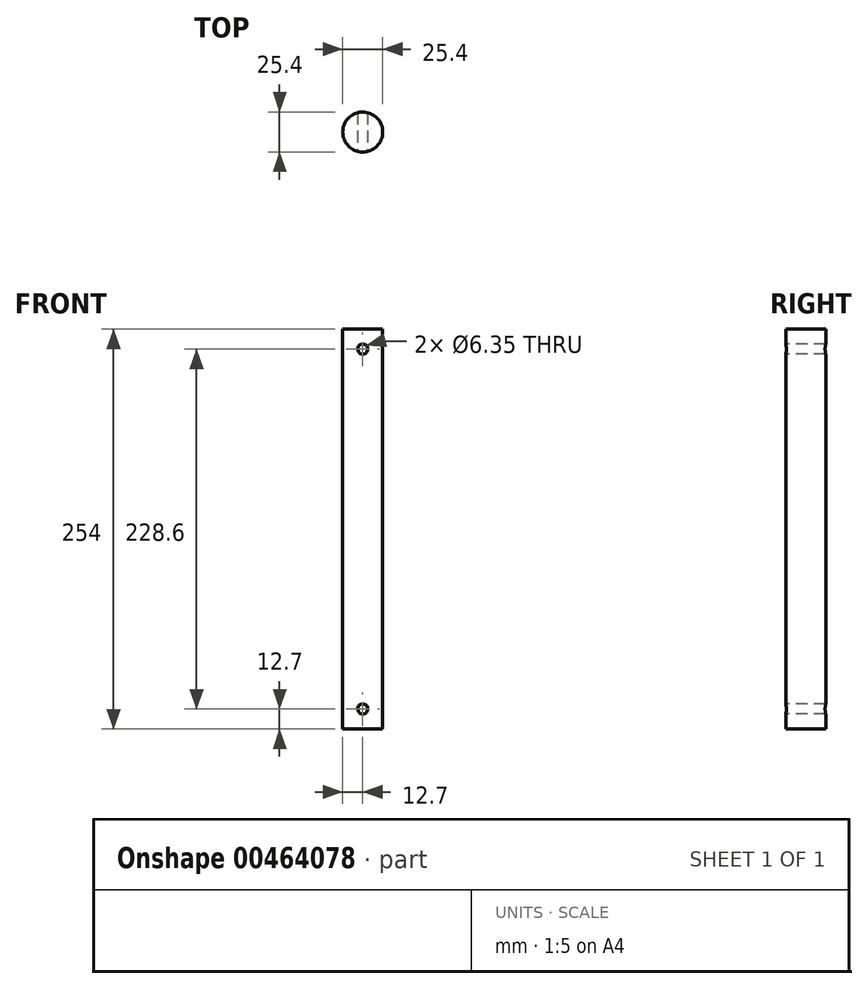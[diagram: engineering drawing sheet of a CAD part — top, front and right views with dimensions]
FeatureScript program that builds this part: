
annotation { "Feature Type Name" : "Feature", "Feature Type Description" : "" }
export const myFeature = defineFeature(function(context is Context, id is Id, definition is map)
    precondition{}
    {
        {
            var Q0;
            Q0=qCreatedBy(makeId("Top.planeOp"),FACE);
            var sketch = newSketch(context, id + "F0", { "sketchPlane" : qUnion([Q0])});
            skCircle(sketch, "E0", {"center": v(0, 0) * mm, "radius": 12.7 * mm});
            skSolve(sketch);
        }
        {
            var Q0;
            Q0 = qSketchRegion(id + "F0", true);
            extrude(context, id + "F1", {"entities" : qUnion([Q0]), "depth" : 254 * mm});
        }
        {
            var Q0;
            Q0=qCreatedBy(makeId("Front.planeOp"),FACE);
            var sketch = newSketch(context, id + "F2", { "sketchPlane" : qUnion([Q0])});
            skLineSegment(sketch, "E1", {"start": v(0, 0) * mm, "end": v(0, 12.7) * mm});
            skCircle(sketch, "E2", {"center": v(0, 12.7) * mm, "radius": 3.18 * mm});
            skSolve(sketch);
        }
        {
            var Q0;
            Q0 = qSketchRegion(id + "F2", true);
            extrude(context, id + "F3", {"entities" : qUnion([Q0]), "operationType" : NewBodyOperationType.REMOVE, "oppositeDirection" : true, "depth" : 25.4 * mm, "hasSecondDirection" : true, "secondDirectionOppositeDirection" : false, "secondDirectionDepth" : 25.4 * mm});
        }
        {
            var Q0;
            Q0=qCreatedBy(makeId("Front.planeOp"),FACE);
            var sketch = newSketch(context, id + "F4", { "sketchPlane" : qUnion([Q0])});
            skLineSegment(sketch, "E3", {"start": v(0, 0) * mm, "end": v(0, 241.3) * mm});
            skCircle(sketch, "E4", {"center": v(0, 241.3) * mm, "radius": 3.18 * mm});
            skSolve(sketch);
        }
        {
            var Q0;
            Q0 = qSketchRegion(id + "F4", true);
            extrude(context, id + "F5", {"entities" : qUnion([Q0]), "operationType" : NewBodyOperationType.REMOVE, "oppositeDirection" : true, "depth" : 25.4 * mm, "hasSecondDirection" : true, "secondDirectionOppositeDirection" : false, "secondDirectionDepth" : 25.4 * mm});
        }
    });
